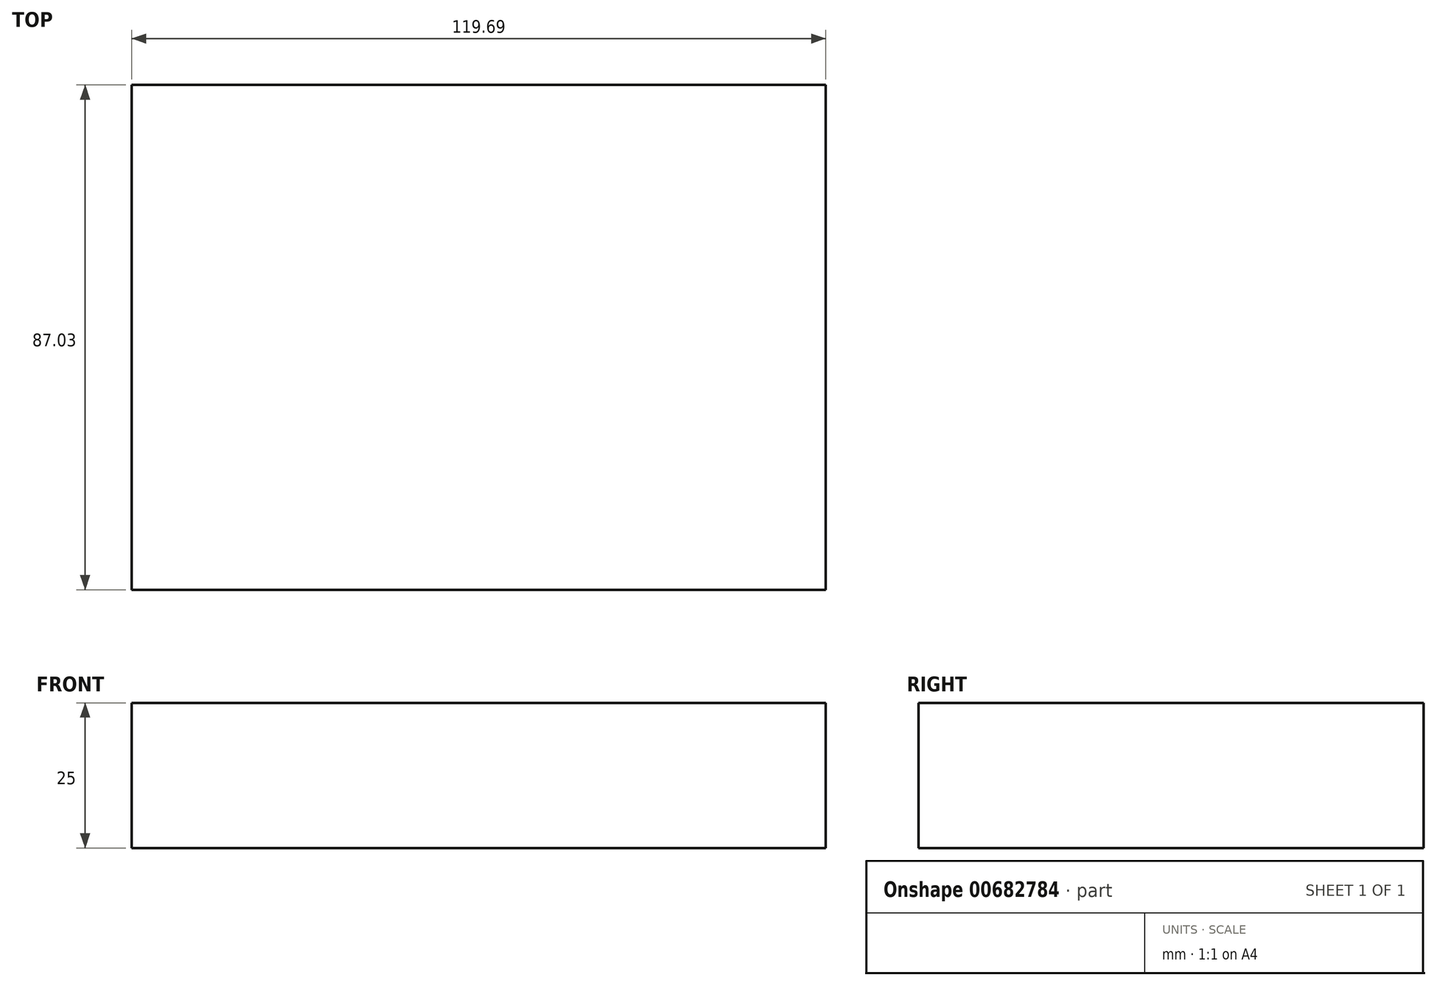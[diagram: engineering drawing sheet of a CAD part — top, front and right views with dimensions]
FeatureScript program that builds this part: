
annotation { "Feature Type Name" : "Feature", "Feature Type Description" : "" }
export const myFeature = defineFeature(function(context is Context, id is Id, definition is map)
    precondition{}
    {
        {
            var Q0;
            Q0=qCreatedBy(makeId("Top.planeOp"),FACE);
            var sketch = newSketch(context, id + "F0", { "sketchPlane" : qUnion([Q0])});
            skLineSegment(sketch, "E0.bottom", {"start": v(-45.88, -45.17) * mm, "end": v(73.81, -45.17) * mm});
            skLineSegment(sketch, "E0.top", {"start": v(-45.88, 41.86) * mm, "end": v(73.81, 41.86) * mm});
            skLineSegment(sketch, "E0.left", {"start": v(-45.88, -45.17) * mm, "end": v(-45.88, 41.86) * mm});
            skLineSegment(sketch, "E0.right", {"start": v(73.81, -45.17) * mm, "end": v(73.81, 41.86) * mm});
            skSolve(sketch);
        }
        {
            var Q0;
            Q0=makeQuery(id+"F0.imprint","IMPRINT",FACE,{"disambiguationData":[TD([[makeQuery(id+"F0.imprint","IMPRINT",EDGE,{"derivedFrom":sQuery(id+"F0.wireOp",EDGE,"E0.bottom")}),1.0]])]});
            extrude(context, id + "F1", {"entities" : qUnion([Q0]), "depth" : 25 * mm, "offsetDistance" : 25 * mm});
        }
    });
